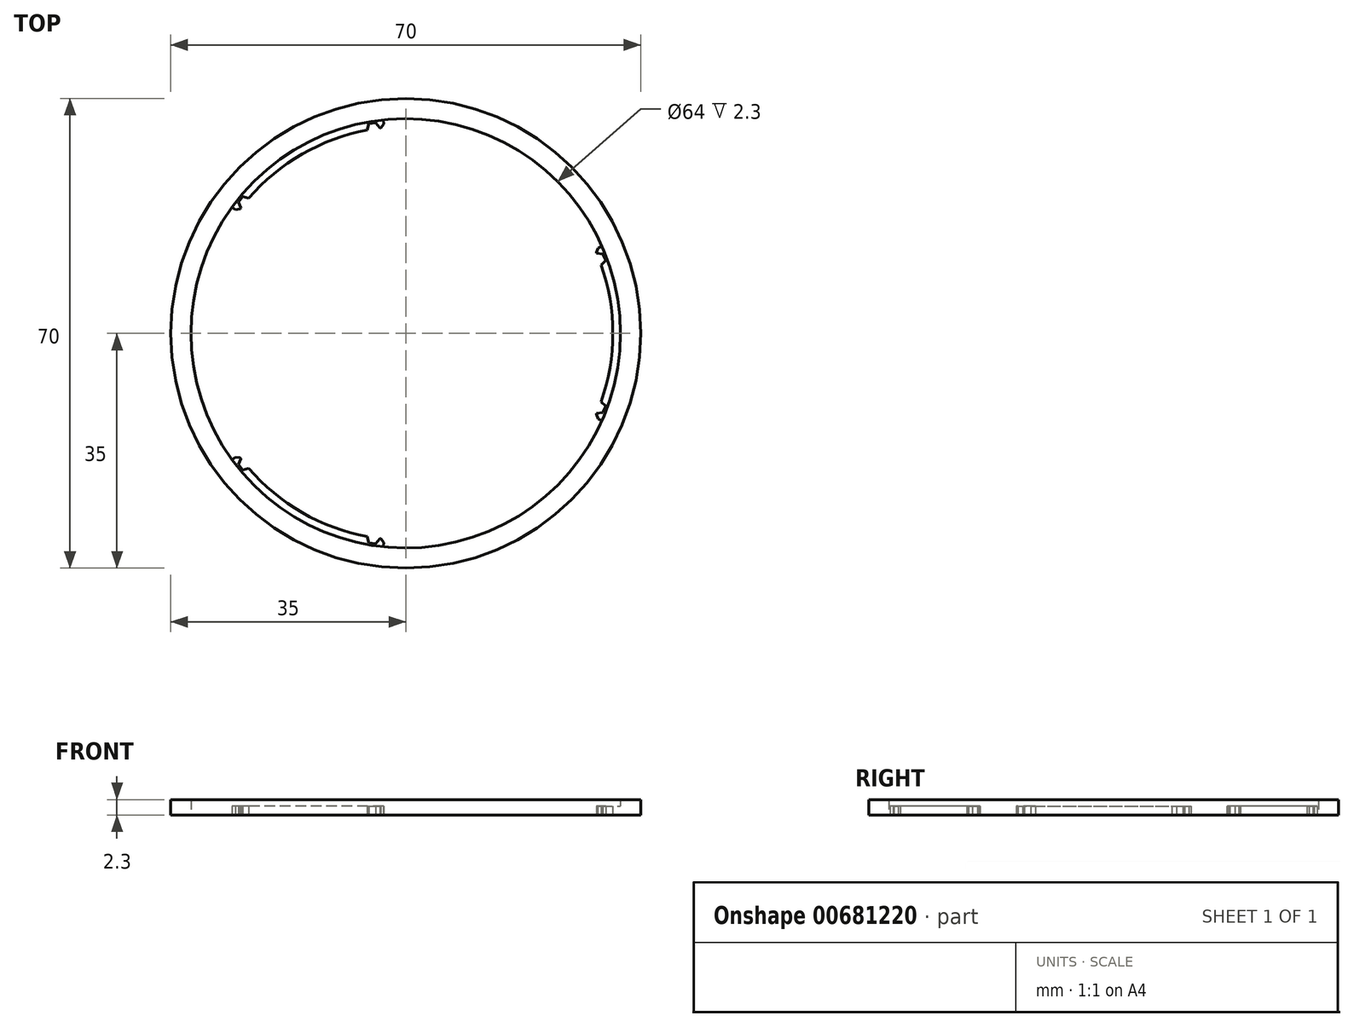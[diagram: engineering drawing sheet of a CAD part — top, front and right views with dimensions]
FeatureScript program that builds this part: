
annotation { "Feature Type Name" : "Feature", "Feature Type Description" : "" }
export const myFeature = defineFeature(function(context is Context, id is Id, definition is map)
    precondition{}
    {
        {
            var Q0;
            Q0=qCreatedBy(makeId("Top.planeOp"),FACE);
            var sketch = newSketch(context, id + "F0", { "sketchPlane" : qUnion([Q0])});
            skArc(sketch, "E0", {"start": v(28.19, -12.53) * mm, "mid": v(30.85, 0) * mm, "end": v(28.19, 12.53) * mm});
            skArc(sketch, "E1", {"start": v(29.24, 13) * mm, "mid": v(16, 27.71) * mm, "end": v(-3.36, 31.82) * mm});
            skLineSegment(sketch, "E2", {"start": v(28.19, 12.53) * mm, "end": v(29.24, 13) * mm});
            skLineSegment(sketch, "E3.MirrorCS", {"start": v(28.19, -12.53) * mm, "end": v(29.24, -13) * mm});
            skArc(sketch, "E4.1.0", {"start": v(-3.24, 30.68) * mm, "mid": v(-15.42, 26.72) * mm, "end": v(-24.95, 18.15) * mm});
            skLineSegment(sketch, "E4.1.1", {"start": v(-3.24, 30.68) * mm, "end": v(-3.36, 31.82) * mm});
            skLineSegment(sketch, "E4.1.2", {"start": v(-24.95, 18.15) * mm, "end": v(-25.88, 18.82) * mm});
            skArc(sketch, "E4.2.0", {"start": v(-24.95, -18.15) * mm, "mid": v(-15.42, -26.72) * mm, "end": v(-3.24, -30.68) * mm});
            skLineSegment(sketch, "E4.2.1", {"start": v(-24.95, -18.15) * mm, "end": v(-25.88, -18.82) * mm});
            skLineSegment(sketch, "E4.2.2", {"start": v(-3.24, -30.68) * mm, "end": v(-3.36, -31.82) * mm});
            skArc(sketch, "E5.trimOffspring", {"start": v(-25.88, 18.82) * mm, "mid": v(-32, 0) * mm, "end": v(-25.88, -18.82) * mm});
            skArc(sketch, "E6.trimOffspring", {"start": v(-3.36, -31.82) * mm, "mid": v(16, -27.71) * mm, "end": v(29.24, -13) * mm});
            skCircle(sketch, "E7", {"center": v(0, 0) * mm, "radius": 35 * mm});
            skSolve(sketch);
        }
        {
            var Q0;
            Q0=makeQuery(id+"F0.imprint","IMPRINT",FACE,{"disambiguationData":[TD([[makeQuery(id+"F0.imprint","IMPRINT",EDGE,{"derivedFrom":sQuery(id+"F0.wireOp",EDGE,"E0")}),-1.0]])]});
            extrude(context, id + "F1", {"entities" : qUnion([Q0]), "depth" : 1.3 * mm, "offsetDistance" : 25 * mm});
        }
        {
            var Q0;
            Q0=makeQuery(id+"F1.opExtrude","CAP_FACE",FACE,{"disambiguationData":[OSD([sQuery(id+"F0.wireOp",EDGE,"E0"),sQuery(id+"F0.wireOp",EDGE,"E1"),sQuery(id+"F0.wireOp",EDGE,"E2"),sQuery(id+"F0.wireOp",EDGE,"E3.MirrorCS"),sQuery(id+"F0.wireOp",EDGE,"E4.1.0"),sQuery(id+"F0.wireOp",EDGE,"E4.1.1"),sQuery(id+"F0.wireOp",EDGE,"E4.1.2"),sQuery(id+"F0.wireOp",EDGE,"E4.2.0"),sQuery(id+"F0.wireOp",EDGE,"E4.2.1"),sQuery(id+"F0.wireOp",EDGE,"E4.2.2"),sQuery(id+"F0.wireOp",EDGE,"E5.trimOffspring"),sQuery(id+"F0.wireOp",EDGE,"E6.trimOffspring"),sQuery(id+"F0.wireOp",EDGE,"E7")])],"isStart":false});
            var sketch = newSketch(context, id + "F2", { "sketchPlane" : qUnion([Q0])});
            skCircle(sketch, "E8", {"center": v(0, 0) * mm, "radius": 32 * mm});
            skCircle(sketch, "E9", {"center": v(0, 0) * mm, "radius": 35 * mm});
            skSolve(sketch);
        }
        {
            var Q0;
            Q0 = qSketchRegion(id + "F2", true);
            extrude(context, id + "F3", {"entities" : qUnion([Q0]), "operationType" : NewBodyOperationType.ADD, "depth" : 1 * mm, "offsetDistance" : 25 * mm});
        }
        {
            var Q0;
            Q0=makeQuery(id+"F1.opExtrude","CAP_FACE",FACE,{"disambiguationData":[OSD([sQuery(id+"F0.wireOp",EDGE,"E0"),sQuery(id+"F0.wireOp",EDGE,"E1"),sQuery(id+"F0.wireOp",EDGE,"E2"),sQuery(id+"F0.wireOp",EDGE,"E3.MirrorCS"),sQuery(id+"F0.wireOp",EDGE,"E4.1.0"),sQuery(id+"F0.wireOp",EDGE,"E4.1.1"),sQuery(id+"F0.wireOp",EDGE,"E4.1.2"),sQuery(id+"F0.wireOp",EDGE,"E4.2.0"),sQuery(id+"F0.wireOp",EDGE,"E4.2.1"),sQuery(id+"F0.wireOp",EDGE,"E4.2.2"),sQuery(id+"F0.wireOp",EDGE,"E5.trimOffspring"),sQuery(id+"F0.wireOp",EDGE,"E6.trimOffspring"),sQuery(id+"F0.wireOp",EDGE,"E7")])],"isStart":true});
            var sketch = newSketch(context, id + "F4", { "sketchPlane" : qUnion([Q0])});
            skLineSegment(sketch, "E10", {"start": v(28.24, 11.99) * mm, "end": v(29.38, 11.8) * mm});
            skLineSegment(sketch, "E11", {"start": v(29.38, 11.8) * mm, "end": v(29.8, 10.87) * mm});
            skLineSegment(sketch, "E12", {"start": v(29.8, 10.87) * mm, "end": v(28.95, 10.01) * mm});
            skLineSegment(sketch, "E13", {"start": v(28.95, 10.01) * mm, "end": v(28.24, 11.99) * mm});
            skLineSegment(sketch, "E14.MirrorCS", {"start": v(29.38, -11.8) * mm, "end": v(29.8, -10.87) * mm});
            skLineSegment(sketch, "E15.MirrorCS", {"start": v(29.8, -10.87) * mm, "end": v(28.95, -10.01) * mm});
            skLineSegment(sketch, "E16.MirrorCS", {"start": v(28.24, -11.99) * mm, "end": v(29.38, -11.8) * mm});
            skLineSegment(sketch, "E17.MirrorCS", {"start": v(28.95, -10.01) * mm, "end": v(28.24, -11.99) * mm});
            skLineSegment(sketch, "E18.1.0", {"start": v(-23.14, 20.06) * mm, "end": v(-24.5, 18.46) * mm});
            skLineSegment(sketch, "E18.1.1", {"start": v(-24.32, 20.37) * mm, "end": v(-23.14, 20.06) * mm});
            skLineSegment(sketch, "E18.1.2", {"start": v(-5.8, 30.08) * mm, "end": v(-3.74, 30.45) * mm});
            skLineSegment(sketch, "E18.1.3", {"start": v(-24.5, 18.46) * mm, "end": v(-24.92, 19.54) * mm});
            skLineSegment(sketch, "E18.1.4", {"start": v(-3.74, 30.45) * mm, "end": v(-4.46, 31.35) * mm});
            skLineSegment(sketch, "E18.1.5", {"start": v(-24.92, 19.54) * mm, "end": v(-24.32, 20.37) * mm});
            skLineSegment(sketch, "E18.1.6", {"start": v(-5.48, 31.24) * mm, "end": v(-5.8, 30.08) * mm});
            skLineSegment(sketch, "E18.1.7", {"start": v(-4.46, 31.35) * mm, "end": v(-5.48, 31.24) * mm});
            skLineSegment(sketch, "E18.2.0", {"start": v(-5.8, -30.08) * mm, "end": v(-3.74, -30.45) * mm});
            skLineSegment(sketch, "E18.2.1", {"start": v(-5.48, -31.24) * mm, "end": v(-5.8, -30.08) * mm});
            skLineSegment(sketch, "E18.2.2", {"start": v(-23.14, -20.06) * mm, "end": v(-24.5, -18.46) * mm});
            skLineSegment(sketch, "E18.2.3", {"start": v(-3.74, -30.45) * mm, "end": v(-4.46, -31.35) * mm});
            skLineSegment(sketch, "E18.2.4", {"start": v(-24.5, -18.46) * mm, "end": v(-24.92, -19.54) * mm});
            skLineSegment(sketch, "E18.2.5", {"start": v(-4.46, -31.35) * mm, "end": v(-5.48, -31.24) * mm});
            skLineSegment(sketch, "E18.2.6", {"start": v(-24.32, -20.37) * mm, "end": v(-23.14, -20.06) * mm});
            skLineSegment(sketch, "E18.2.7", {"start": v(-24.92, -19.54) * mm, "end": v(-24.32, -20.37) * mm});
            skPoint(sketch, "E18.center", {"position": v(0, 0) * mm});
            skSolve(sketch);
        }
        {
            var Q0;
            Q0 = qSketchRegion(id + "F4", true);
            extrude(context, id + "F5", {"entities" : qUnion([Q0]), "operationType" : NewBodyOperationType.REMOVE, "oppositeDirection" : true, "depth" : 25 * mm, "offsetDistance" : 25 * mm});
        }
        {
            var Q0;
            Q0=makeQuery(id+"F1.opExtrude","SWEPT_EDGE",EDGE,{"disambiguationData":[OSD([sQuery(id+"F0.wireOp",EDGE,"E4.2.0"),sQuery(id+"F0.wireOp",EDGE,"E4.2.2")])]});
            var Q1;
            Q1=makeQuery(id+"F1.opExtrude","SWEPT_EDGE",EDGE,{"disambiguationData":[OSD([sQuery(id+"F0.wireOp",EDGE,"E4.2.0"),sQuery(id+"F0.wireOp",EDGE,"E4.2.1")])]});
            var Q2;
            Q2=makeQuery(id+"F1.opExtrude","SWEPT_EDGE",EDGE,{"disambiguationData":[OSD([sQuery(id+"F0.wireOp",EDGE,"E4.1.0"),sQuery(id+"F0.wireOp",EDGE,"E4.1.2")])]});
            var Q3;
            Q3=makeQuery(id+"F1.opExtrude","SWEPT_EDGE",EDGE,{"disambiguationData":[OSD([sQuery(id+"F0.wireOp",EDGE,"E4.1.0"),sQuery(id+"F0.wireOp",EDGE,"E4.1.1")])]});
            var Q4;
            Q4=makeQuery(id+"F1.opExtrude","SWEPT_EDGE",EDGE,{"disambiguationData":[OSD([sQuery(id+"F0.wireOp",EDGE,"E0"),sQuery(id+"F0.wireOp",EDGE,"E2")])]});
            var Q5;
            Q5=makeQuery(id+"F1.opExtrude","SWEPT_EDGE",EDGE,{"disambiguationData":[OSD([sQuery(id+"F0.wireOp",EDGE,"E0"),sQuery(id+"F0.wireOp",EDGE,"E3.MirrorCS")])]});
            chamfer(context, id + "F6", {"entities" : qUnion([Q0, Q1, Q2, Q3, Q4, Q5]), "width" : 0.5 * mm, "tangentPropagation" : true});
        }
    });
